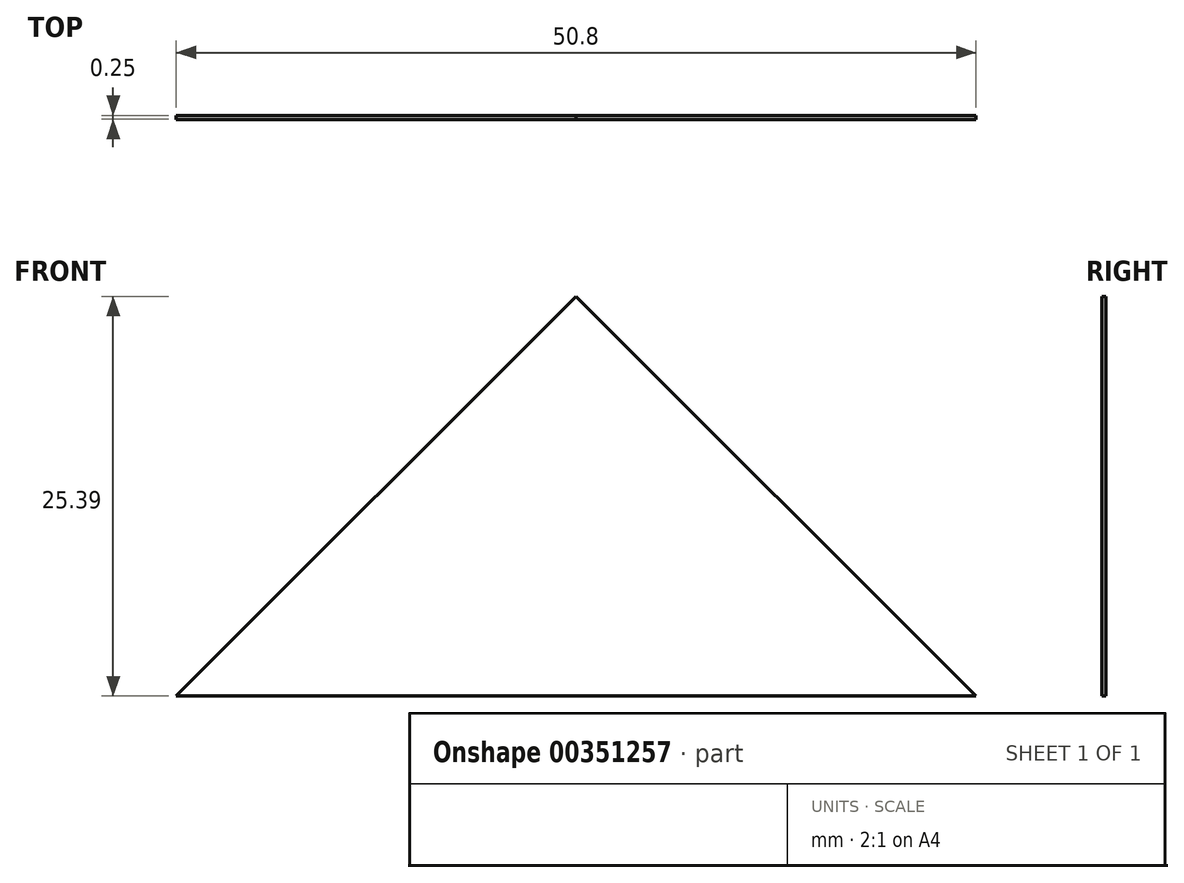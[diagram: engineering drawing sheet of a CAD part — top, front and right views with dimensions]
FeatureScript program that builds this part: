
annotation { "Feature Type Name" : "Feature", "Feature Type Description" : "" }
export const myFeature = defineFeature(function(context is Context, id is Id, definition is map)
    precondition{}
    {
        {
            var Q0;
            Q0=qCreatedBy(makeId("Front.planeOp"),FACE);
            var sketch = newSketch(context, id + "F0", { "sketchPlane" : qUnion([Q0])});
            skLineSegment(sketch, "E0", {"start": v(-65.4, 0) * mm, "end": v(-14.6, 0) * mm});
            skLineSegment(sketch, "E1", {"start": v(-65.4, 0) * mm, "end": v(-40, 25.4) * mm});
            skLineSegment(sketch, "E2", {"start": v(-14.6, 0) * mm, "end": v(-40, 25.4) * mm});
            skSolve(sketch);
        }
        {
            var Q0;
            Q0=makeQuery(id+"F0.imprint","IMPRINT",FACE,{"disambiguationData":[TD([[makeQuery(id+"F0.imprint","IMPRINT",EDGE,{"derivedFrom":sQuery(id+"F0.wireOp",EDGE,"E0")}),1.0]])]});
            extrude(context, id + "F1", {"entities" : qUnion([Q0]), "depth" : 0.25 * mm});
        }
    });
